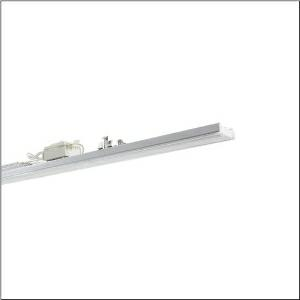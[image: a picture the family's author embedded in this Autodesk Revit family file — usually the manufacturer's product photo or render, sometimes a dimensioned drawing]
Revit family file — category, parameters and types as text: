
# Revit family: licross_11_recessed_ho_51tl12dv4m2m3s4
name_source: partatom
category: Lighting Fixtures
units: mm (PartAtom-declared; Revit-internal decimal feet)

## family parameters
Cut with Voids When Loaded = No
Host = Face
Light Source = No
Part Type = Normal
Room Calculation Point = No
Round Connector Dimension = Use Diameter
Shared = No

## types (1)
- --- (1 x LED, 1010 lm, 5.9 W, 4000K)
    Apparent Load = 6 VA
    CIE Flux Codes = 66 91 98 100 100
    Color Rendering = 80
    Color Temperature = 4000K
    Default Elevation = 1800 mm
    Description = Licross 11 Recessed HO, luminaire insert, of sheet steel, coil coated, white, length: 2.250mm, width: 66mm, height: 67mm, LED rated luminous flux: 27.150lm, light colour: 840, SDCM (Standard Deviation of Colour Matching)MacAdam ≤ 2 SDCM (initial), control gear: DALI 2, with plug, 6-pole, with phase selection, for trunking rail, 9 or 11-core, mains connection: 220..240V, AC, 50/60Hz, rated input power: 154W, for trunking rail, 9-/11-core, internal wiring halogen-free, for emergency light function, converter,control gear: single battery element, battery: LiFePO4, 9Ah, primary optical cover: cover, of PMMA, light emission: direct distribution, primary light characteristic: symmetric, protection rating (complete): IP40, insulation class (complete): insulation class I (protective earthing), certification: CE, UKCA, protection symbol: D if used in an environment without relevant dust loads with corresponding accessories, impact resistance: IK06, permissible ambient temperature for indoor applications: +5..+35°C, standard: EN 60598-2-22, LABS conformity tested according to VDMA 24364:2018-05, reducing of maximum allowable ambient temperature of 5°C with ceiling mounting, corresponds to IFS (International Featured Standards) requirements for safety and quality in the food industry, The light source and the operating device comply with the requirements of the Ecodesign Regulation (EU) 2019/2020 and are replaceable in accordance with this regulation, packaging unit: 1 piece
    Height = 58 mm
    Lamp = 1 x LED
    Lamp Light Flux = 1010 lm
    Lamp Power = 5.9 W
    Lamp count = 1
    Length = 2250 mm
    Luminous efficacy = 171 lm/W
    Manufacturer = Siteco
    ModVariant = No
    Model = 51TL12DV4M2M3S4
    Mounting Place = Ceiling
    Mounting Type = Pendant
    Number of Poles = 1
    OnlyDefault = Yes
    Power Factor = 1
    Product Name = Licross 11 Recessed HO
    Product group = luminaire insert | ceiling pendant
    ProductGroupID = 901
    Protection Class = Protection class I
    Protection Degree = IP 40
    RLX_Detail_Level = 1
    RLX_Emergency_Light_Flux = 0 lm
    RLX_Emergency_Type = 0
    RLX_Emergency_Type_DB = No
    RlxData = <blob elided: 30213 chars, md5=0dc2e929>
    Socket = socket
    Standby Power = 0 W
    System Light Flux = 1010 lm
    System Power = 6 W
    Type Comments = : emergency light operation: 3 h
    Type Image = l_1296930.jpg
    URL = http://relux.com
    VarID = @adj_089617
    Voltage = 0 V
    Weight = 0.00 kg
    Width = 66 mm

## geometry (parser evidence)
native form markers: Blend x4, Sweep x11
no freeform markers — native parametric forms only
